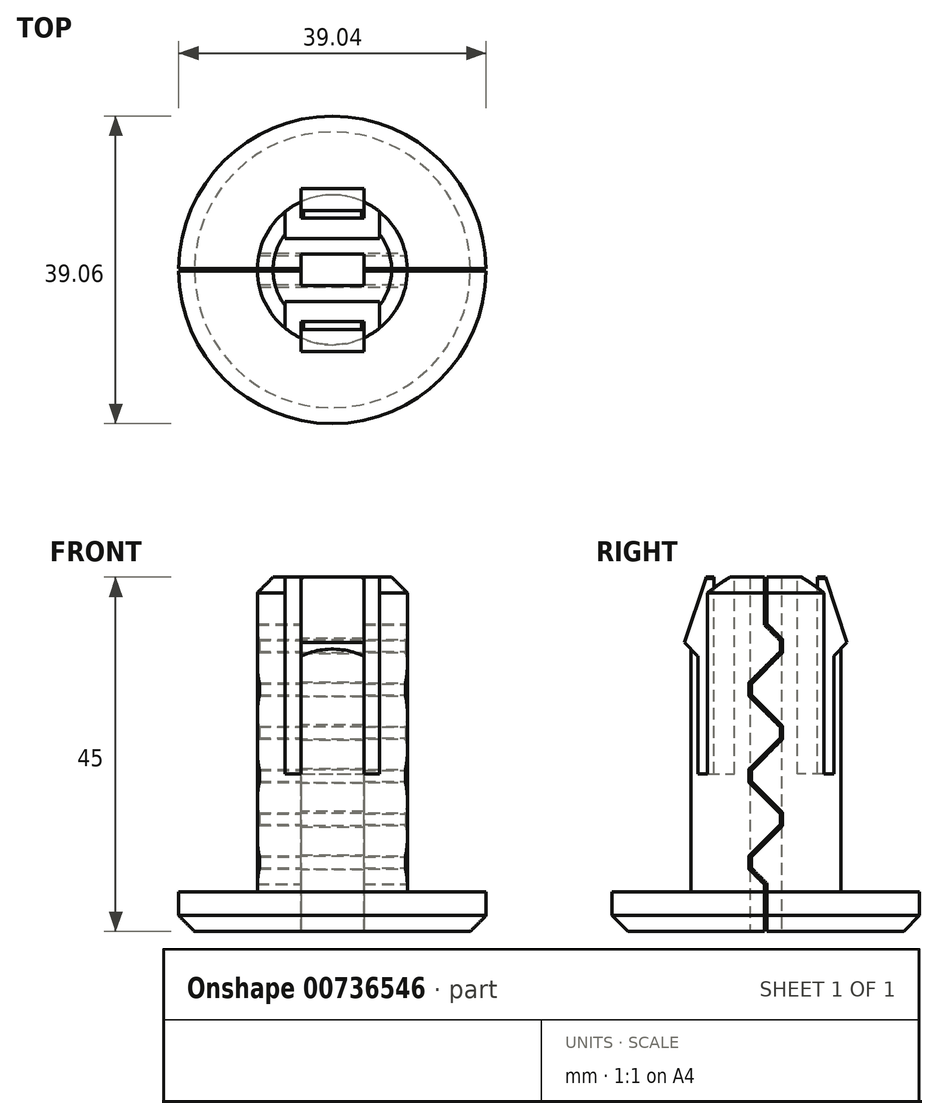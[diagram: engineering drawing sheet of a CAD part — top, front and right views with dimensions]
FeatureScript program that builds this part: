
annotation { "Feature Type Name" : "Feature", "Feature Type Description" : "" }
export const myFeature = defineFeature(function(context is Context, id is Id, definition is map)
    precondition{}
    {
        {
            assignVariable(context, id + "F0", {"name" : "Depth", "anyValue" : 45 * mm});
        }
        {
            var Q0;
            Q0=qCreatedBy(makeId("Front.planeOp"),FACE);
            var sketch = newSketch(context, id + "F1", { "sketchPlane" : qUnion([Q0])});
            skLineSegment(sketch, "E0", {"start": v(0, 0) * mm, "end": v(0, 45) * mm});
            skLineSegment(sketch, "E1", {"start": v(0, 45) * mm, "end": v(9.53, 45) * mm});
            skLineSegment(sketch, "E2", {"start": v(9.53, 45) * mm, "end": v(9.53, 5) * mm});
            skLineSegment(sketch, "E3", {"start": v(9.53, 5) * mm, "end": v(19.53, 5) * mm});
            skLineSegment(sketch, "E4", {"start": v(19.53, 5) * mm, "end": v(19.53, 0) * mm});
            skLineSegment(sketch, "E5", {"start": v(19.53, 0) * mm, "end": v(0, 0) * mm});
            skSolve(sketch);
        }
        {
            var Q0;
            Q0=makeQuery(id+"F1.imprint","IMPRINT",FACE,{"disambiguationData":[TD([[makeQuery(id+"F1.imprint","IMPRINT",EDGE,{"derivedFrom":sQuery(id+"F1.wireOp",EDGE,"E0")}),-1.0]])]});
            var Q1;
            Q1=sQuery(id+"F1.wireOp",EDGE,"E0");
            revolve(context, id + "F2", {"surfaceOperationType" : NewSurfaceOperationType.NEW, "entities" : qUnion([Q0]), "axis" : qUnion([Q1]), "revolveType" : RevolveType.FULL});
        }
        {
            var Q0;
            Q0=makeQuery(id+"F2.opRevolve","SWEPT_FACE",FACE,{"disambiguationData":[OSD([sQuery(id+"F1.wireOp",EDGE,"E5")])]});
            var sketch = newSketch(context, id + "F3", { "sketchPlane" : qUnion([Q0])});
            skLineSegment(sketch, "E6.bottom", {"start": v(4, -2) * mm, "end": v(-4, -2) * mm});
            skLineSegment(sketch, "E6.top", {"start": v(4, 2) * mm, "end": v(-4, 2) * mm});
            skLineSegment(sketch, "E6.left", {"start": v(4, -2) * mm, "end": v(4, 2) * mm});
            skLineSegment(sketch, "E6.right", {"start": v(-4, -2) * mm, "end": v(-4, 2) * mm});
            skPoint(sketch, "E6.middle", {"position": v(0, 0) * mm});
            skSolve(sketch);
        }
        {
            var Q0;
            Q0=makeQuery(id+"F3.imprint","IMPRINT",FACE,{"disambiguationData":[TD([[makeQuery(id+"F3.imprint","IMPRINT",EDGE,{"derivedFrom":sQuery(id+"F3.wireOp",EDGE,"E6.bottom")}),-1.0]])]});
            extrude(context, id + "F4", {"entities" : qUnion([Q0]), "operationType" : NewBodyOperationType.REMOVE, "endBound" : BoundingType.THROUGH_ALL, "oppositeDirection" : true, "depth" : 25 * mm, "offsetDistance" : 25 * mm});
        }
        {
            var Q0;
            Q0=makeQuery(id+"F2.opRevolve","SWEPT_EDGE",EDGE,{"disambiguationData":[OSD([sQuery(id+"F1.wireOp",EDGE,"E4"),sQuery(id+"F1.wireOp",EDGE,"E5")])]});
            chamfer(context, id + "F5", {"entities" : qUnion([Q0]), "width" : 2 * mm, "tangentPropagation" : true});
        }
        {
            var Q0;
            Q0=makeQuery(id+"F2.opRevolve","SWEPT_EDGE",EDGE,{"disambiguationData":[OSD([sQuery(id+"F1.wireOp",EDGE,"E1"),sQuery(id+"F1.wireOp",EDGE,"E2")])]});
            chamfer(context, id + "F6", {"entities" : qUnion([Q0]), "width" : 2 * mm, "tangentPropagation" : true});
        }
        {
            var Q0;
            Q0=qCreatedBy(makeId("Right.planeOp"),FACE);
            var sketch = newSketch(context, id + "F7", { "sketchPlane" : qUnion([Q0])});
            skLineSegment(sketch, "E7.0", {"start": v(-7.53, 45) * mm, "end": v(7.53, 45) * mm, "construction": true});
            skLineSegment(sketch, "E8", {"start": v(0, 0) * mm, "end": v(0, 6) * mm});
            skLineSegment(sketch, "E9", {"start": v(0, 6) * mm, "end": v(-2, 8) * mm});
            skLineSegment(sketch, "E10", {"start": v(-2, 8) * mm, "end": v(-2, 9.5) * mm});
            skLineSegment(sketch, "E11", {"start": v(-2, 9.5) * mm, "end": v(2, 13.5) * mm});
            skLineSegment(sketch, "E12", {"start": v(2, 13.5) * mm, "end": v(2, 15) * mm});
            skLineSegment(sketch, "E13", {"start": v(2, 15) * mm, "end": v(-2, 19) * mm});
            skLineSegment(sketch, "E14", {"start": v(-2, 19) * mm, "end": v(-2, 20.5) * mm});
            skLineSegment(sketch, "E15", {"start": v(-2, 20.5) * mm, "end": v(2, 24.5) * mm});
            skLineSegment(sketch, "E16", {"start": v(2, 24.5) * mm, "end": v(2, 26) * mm});
            skLineSegment(sketch, "E17", {"start": v(2, 26) * mm, "end": v(-2, 30) * mm});
            skLineSegment(sketch, "E18", {"start": v(-2, 30) * mm, "end": v(-2, 31.5) * mm});
            skLineSegment(sketch, "E19", {"start": v(-2, 31.5) * mm, "end": v(2, 35.5) * mm});
            skLineSegment(sketch, "E20", {"start": v(2, 35.5) * mm, "end": v(2, 37) * mm});
            skLineSegment(sketch, "E21", {"start": v(2, 37) * mm, "end": v(0, 39) * mm});
            skLineSegment(sketch, "E22", {"start": v(0, 39) * mm, "end": v(0, 45) * mm});
            skPoint(sketch, "E23", {"position": v(0, 11.5) * mm});
            skLineSegment(sketch, "E24.0", {"start": v(0.15, 39.06) * mm, "end": v(0.15, 45) * mm});
            skLineSegment(sketch, "E24.1", {"start": v(2.15, 37.06) * mm, "end": v(0.15, 39.06) * mm});
            skLineSegment(sketch, "E24.2", {"start": v(2.15, 35.44) * mm, "end": v(2.15, 37.06) * mm});
            skLineSegment(sketch, "E24.3", {"start": v(-1.85, 31.44) * mm, "end": v(2.15, 35.44) * mm});
            skLineSegment(sketch, "E24.4", {"start": v(-1.85, 30.06) * mm, "end": v(-1.85, 31.44) * mm});
            skLineSegment(sketch, "E24.5", {"start": v(-1.85, 9.44) * mm, "end": v(2.15, 13.44) * mm});
            skLineSegment(sketch, "E24.6", {"start": v(-1.85, 8.06) * mm, "end": v(-1.85, 9.44) * mm});
            skLineSegment(sketch, "E24.7", {"start": v(0.15, 6.06) * mm, "end": v(-1.85, 8.06) * mm});
            skLineSegment(sketch, "E24.8", {"start": v(0.15, 0) * mm, "end": v(0.15, 6.06) * mm});
            skLineSegment(sketch, "E24.9", {"start": v(2.15, 13.44) * mm, "end": v(2.15, 15.06) * mm});
            skLineSegment(sketch, "E24.10", {"start": v(2.15, 15.06) * mm, "end": v(-1.85, 19.06) * mm});
            skLineSegment(sketch, "E24.11", {"start": v(-1.85, 19.06) * mm, "end": v(-1.85, 20.44) * mm});
            skLineSegment(sketch, "E24.12", {"start": v(-1.85, 20.44) * mm, "end": v(2.15, 24.44) * mm});
            skLineSegment(sketch, "E24.13", {"start": v(2.15, 24.44) * mm, "end": v(2.15, 26.06) * mm});
            skLineSegment(sketch, "E24.14", {"start": v(2.15, 26.06) * mm, "end": v(-1.85, 30.06) * mm});
            skLineSegment(sketch, "E25.0", {"start": v(-0.15, 38.94) * mm, "end": v(-0.15, 45) * mm});
            skLineSegment(sketch, "E25.1", {"start": v(1.85, 36.94) * mm, "end": v(-0.15, 38.94) * mm});
            skLineSegment(sketch, "E25.2", {"start": v(1.85, 35.56) * mm, "end": v(1.85, 36.94) * mm});
            skLineSegment(sketch, "E25.3", {"start": v(-2.15, 31.56) * mm, "end": v(1.85, 35.56) * mm});
            skLineSegment(sketch, "E25.4", {"start": v(-2.15, 29.94) * mm, "end": v(-2.15, 31.56) * mm});
            skLineSegment(sketch, "E25.5", {"start": v(-2.15, 9.56) * mm, "end": v(1.85, 13.56) * mm});
            skLineSegment(sketch, "E25.6", {"start": v(-2.15, 7.94) * mm, "end": v(-2.15, 9.56) * mm});
            skLineSegment(sketch, "E25.7", {"start": v(-0.15, 5.94) * mm, "end": v(-2.15, 7.94) * mm});
            skLineSegment(sketch, "E25.8", {"start": v(-0.15, 0) * mm, "end": v(-0.15, 5.94) * mm});
            skLineSegment(sketch, "E25.9", {"start": v(1.85, 13.56) * mm, "end": v(1.85, 14.94) * mm});
            skLineSegment(sketch, "E25.10", {"start": v(1.85, 14.94) * mm, "end": v(-2.15, 18.94) * mm});
            skLineSegment(sketch, "E25.11", {"start": v(-2.15, 18.94) * mm, "end": v(-2.15, 20.56) * mm});
            skLineSegment(sketch, "E25.12", {"start": v(-2.15, 20.56) * mm, "end": v(1.85, 24.56) * mm});
            skLineSegment(sketch, "E25.13", {"start": v(1.85, 24.56) * mm, "end": v(1.85, 25.94) * mm});
            skLineSegment(sketch, "E25.14", {"start": v(1.85, 25.94) * mm, "end": v(-2.15, 29.94) * mm});
            skLineSegment(sketch, "E26", {"start": v(-0.15, 45) * mm, "end": v(0.15, 45) * mm});
            skLineSegment(sketch, "E27", {"start": v(-0.15, 0) * mm, "end": v(0.15, 0) * mm});
            skSolve(sketch);
        }
        {
            var Q0;
            {var subQ1=sQuery(id+"F7.wireOp",EDGE,"E8");Q0=makeQuery(id+"F7.imprint","IMPRINT",FACE,{"disambiguationData":[TD([[makeQuery(id+"F7.imprint","IMPRINT",EDGE,{"derivedFrom":subQ1}),1.0]])]});}
            var Q1;
            {var subQ3=sQuery(id+"F7.wireOp",EDGE,"E8");Q1=makeQuery(id+"F7.imprint","IMPRINT",FACE,{"disambiguationData":[TD([[makeQuery(id+"F7.imprint","IMPRINT",EDGE,{"derivedFrom":subQ3}),-1.0]])]});}
            extrude(context, id + "F8", {"entities" : qUnion([Q0, Q1]), "operationType" : NewBodyOperationType.REMOVE, "endBound" : BoundingType.THROUGH_ALL, "oppositeDirection" : true, "depth" : 25 * mm, "offsetDistance" : 25 * mm, "hasSecondDirection" : true, "secondDirectionBound" : SecondDirectionBoundingType.THROUGH_ALL, "secondDirectionOppositeDirection" : false, "secondDirectionDepth" : 25 * mm});
        }
        {
            var Q0;
            {var subQ0=sQuery(id+"F1.wireOp",EDGE,"E1");Q0=makeQuery(id+"F8.boolean.opBoolean","SPLIT",FACE,{"disambiguationData":[TD([makeQuery(id+"F4.boolean.opBoolean","COPY",FACE,{"derivedFrom":makeQuery(id+"F4.opExtrude","SWEPT_FACE",FACE,{"disambiguationData":[OSD([sQuery(id+"F3.wireOp",EDGE,"E6.top")])]})})])],"derivedFrom":makeQuery(id+"F2.opRevolve","SWEPT_FACE",FACE,{"disambiguationData":[OSD([subQ0])]})});}
            var sketch = newSketch(context, id + "F9", { "sketchPlane" : qUnion([Q0])});
            skArc(sketch, "E28.0", {"start": v(9.52, -0.15) * mm, "mid": v(0, -9.53) * mm, "end": v(-9.52, -0.15) * mm});
            skArc(sketch, "E28.1", {"start": v(-9.52, 0.15) * mm, "mid": v(0, 9.53) * mm, "end": v(9.52, 0.15) * mm});
            skLineSegment(sketch, "E29.2", {"start": v(4, -2) * mm, "end": v(-4, -2) * mm, "construction": true});
            skLineSegment(sketch, "E29.3", {"start": v(4, 2) * mm, "end": v(-4, 2) * mm, "construction": true});
            skLineSegment(sketch, "E30", {"start": v(-4, -8.64) * mm, "end": v(-4, -6.57) * mm});
            skLineSegment(sketch, "E31", {"start": v(-4, -6.57) * mm, "end": v(0, -6.57) * mm});
            skLineSegment(sketch, "E32", {"start": v(-6, -7.4) * mm, "end": v(-6, -4) * mm});
            skLineSegment(sketch, "E33", {"start": v(-6, -4) * mm, "end": v(0, -4) * mm});
            skLineSegment(sketch, "E34.MirrorCS", {"start": v(4, -6.57) * mm, "end": v(0, -6.57) * mm});
            skLineSegment(sketch, "E35.MirrorCS", {"start": v(6, -4) * mm, "end": v(0, -4) * mm});
            skLineSegment(sketch, "E36.MirrorCS", {"start": v(4, -8.64) * mm, "end": v(4, -6.57) * mm});
            skLineSegment(sketch, "E37.MirrorCS", {"start": v(6, -7.4) * mm, "end": v(6, -4) * mm});
            skLineSegment(sketch, "E38.MirrorCS", {"start": v(-4, 6.57) * mm, "end": v(0, 6.57) * mm});
            skLineSegment(sketch, "E39.MirrorCS", {"start": v(4, 6.57) * mm, "end": v(0, 6.57) * mm});
            skLineSegment(sketch, "E40.MirrorCS", {"start": v(4, 8.64) * mm, "end": v(4, 6.57) * mm});
            skLineSegment(sketch, "E41.MirrorCS", {"start": v(6, 7.4) * mm, "end": v(6, 4) * mm});
            skLineSegment(sketch, "E42.MirrorCS", {"start": v(6, 4) * mm, "end": v(0, 4) * mm});
            skLineSegment(sketch, "E43.MirrorCS", {"start": v(-6, 4) * mm, "end": v(0, 4) * mm});
            skLineSegment(sketch, "E44.MirrorCS", {"start": v(-4, 8.64) * mm, "end": v(-4, 6.57) * mm});
            skLineSegment(sketch, "E45.MirrorCS", {"start": v(-6, 7.4) * mm, "end": v(-6, 4) * mm});
            skSolve(sketch);
        }
        {
            var Q0;
            Q0=makeQuery(id+"F9.imprint","IMPRINT",FACE,{"disambiguationData":[TD([[makeQuery(id+"F9.imprint","IMPRINT",EDGE,{"derivedFrom":sQuery(id+"F9.wireOp",EDGE,"E38.MirrorCS")}),-1.0]])]});
            var Q1;
            {var subQ8=sQuery(id+"F9.wireOp",EDGE,"E30");Q1=makeQuery(id+"F9.imprint","IMPRINT",FACE,{"disambiguationData":[TD([[makeQuery(id+"F9.imprint","IMPRINT",EDGE,{"derivedFrom":subQ8}),1.0]])]});}
            var Q2;
            {var subQ0=sQuery(id+"F9.wireOp",EDGE,"E33");Q2=makeQuery(id+"F9.imprint","IMPRINT",FACE,{"disambiguationData":[TD([[makeQuery(id+"F9.imprint","IMPRINT",EDGE,{"derivedFrom":subQ0}),-1.0]])]});}
            var Q3;
            {var subQ8=sQuery(id+"F9.wireOp",EDGE,"E36.MirrorCS");Q3=makeQuery(id+"F9.imprint","IMPRINT",FACE,{"disambiguationData":[TD([[makeQuery(id+"F9.imprint","IMPRINT",EDGE,{"derivedFrom":subQ8}),-1.0]])]});}
            extrude(context, id + "F10", {"entities" : qUnion([Q0, Q1, Q2, Q3]), "operationType" : NewBodyOperationType.REMOVE, "oppositeDirection" : true, "depth" : getVariable(context, 'Depth') - 20 * mm, "offsetDistance" : 25 * mm});
        }
        {
            var Q0;
            Q0=makeQuery(id+"F10.boolean.opBoolean","COPY",FACE,{"derivedFrom":makeQuery(id+"F10.opExtrude","SWEPT_FACE",FACE,{"disambiguationData":[OSD([sQuery(id+"F9.wireOp",EDGE,"E31"),sQuery(id+"F9.wireOp",EDGE,"E34.MirrorCS")])]})});
            var sketch = newSketch(context, id + "F11", { "sketchPlane" : qUnion([Q0])});
            skLineSegment(sketch, "E46", {"start": v(4, 44.84) * mm, "end": v(3.68, 45) * mm});
            skLineSegment(sketch, "E47", {"start": v(3.68, 45) * mm, "end": v(-3.68, 45) * mm});
            skLineSegment(sketch, "E48", {"start": v(-3.68, 45) * mm, "end": v(-4, 44.84) * mm});
            skLineSegment(sketch, "E49", {"start": v(-4, 44.84) * mm, "end": v(-4, 35) * mm});
            skLineSegment(sketch, "E50", {"start": v(-4, 35) * mm, "end": v(4, 35) * mm});
            skLineSegment(sketch, "E51", {"start": v(4, 35) * mm, "end": v(4, 44.84) * mm});
            skSolve(sketch);
        }
        {
            var Q0;
            Q0=makeQuery(id+"F11.imprint","IMPRINT",FACE,{"disambiguationData":[TD([[makeQuery(id+"F11.imprint","IMPRINT",EDGE,{"derivedFrom":sQuery(id+"F11.wireOp",EDGE,"E46")}),1.0]])]});
            extrude(context, id + "F12", {"entities" : qUnion([Q0]), "operationType" : NewBodyOperationType.ADD, "oppositeDirection" : true, "depth" : 6 * mm, "offsetDistance" : 25 * mm});
        }
        {
            var Q0;
            Q0=makeQuery(id+"F12.opExtrude","CAP_EDGE",EDGE,{"disambiguationData":[OSD([sQuery(id+"F11.wireOp",EDGE,"E50")])],"isStart":false});
            chamfer(context, id + "F13", {"entities" : qUnion([Q0]), "width" : 3.9 * mm, "tangentPropagation" : true});
        }
        {
            var Q0;
            Q0=makeQuery(id+"F12.opExtrude","CAP_EDGE",EDGE,{"disambiguationData":[OSD([sQuery(id+"F11.wireOp",EDGE,"E47")])],"isStart":false});
            chamfer(context, id + "F14", {"entities" : qUnion([Q0]), "chamferType" : ChamferType.TWO_OFFSETS, "width1" : 5 * mm, "oppositeDirection" : false, "width2" : 15 * mm, "tangentPropagation" : true});
        }
        {
            var Q0;
            Q0=makeQuery(id+"F10.boolean.opBoolean","COPY",FACE,{"derivedFrom":makeQuery(id+"F10.opExtrude","SWEPT_FACE",FACE,{"disambiguationData":[OSD([sQuery(id+"F9.wireOp",EDGE,"E38.MirrorCS"),sQuery(id+"F9.wireOp",EDGE,"E39.MirrorCS")])]})});
            var sketch = newSketch(context, id + "F15", { "sketchPlane" : qUnion([Q0])});
            skLineSegment(sketch, "E52", {"start": v(-3.68, 45) * mm, "end": v(3.68, 45) * mm});
            skLineSegment(sketch, "E53", {"start": v(3.68, 45) * mm, "end": v(4, 44.84) * mm});
            skLineSegment(sketch, "E54", {"start": v(4, 44.84) * mm, "end": v(4, 35) * mm});
            skLineSegment(sketch, "E55", {"start": v(4, 35) * mm, "end": v(-4, 35) * mm});
            skLineSegment(sketch, "E56", {"start": v(-4, 35) * mm, "end": v(-4, 44.84) * mm});
            skLineSegment(sketch, "E57", {"start": v(-4, 44.84) * mm, "end": v(-3.68, 45) * mm});
            skSolve(sketch);
        }
        {
            var Q0;
            Q0=makeQuery(id+"F15.imprint","IMPRINT",FACE,{"disambiguationData":[TD([[makeQuery(id+"F15.imprint","IMPRINT",EDGE,{"derivedFrom":sQuery(id+"F15.wireOp",EDGE,"E52")}),1.0]])]});
            extrude(context, id + "F16", {"entities" : qUnion([Q0]), "operationType" : NewBodyOperationType.ADD, "oppositeDirection" : true, "depth" : 6 * mm, "offsetDistance" : 25 * mm});
        }
        {
            var Q0;
            Q0=makeQuery(id+"F16.opExtrude","CAP_EDGE",EDGE,{"disambiguationData":[OSD([sQuery(id+"F15.wireOp",EDGE,"E55")])],"isStart":false});
            chamfer(context, id + "F17", {"entities" : qUnion([Q0]), "width" : 3.9 * mm, "tangentPropagation" : true});
        }
        {
            var Q0;
            Q0=makeQuery(id+"F16.opExtrude","CAP_EDGE",EDGE,{"disambiguationData":[OSD([sQuery(id+"F15.wireOp",EDGE,"E52")])],"isStart":false});
            chamfer(context, id + "F18", {"entities" : qUnion([Q0]), "chamferType" : ChamferType.TWO_OFFSETS, "width1" : 5 * mm, "oppositeDirection" : false, "width2" : 15 * mm, "tangentPropagation" : true});
        }
    });
